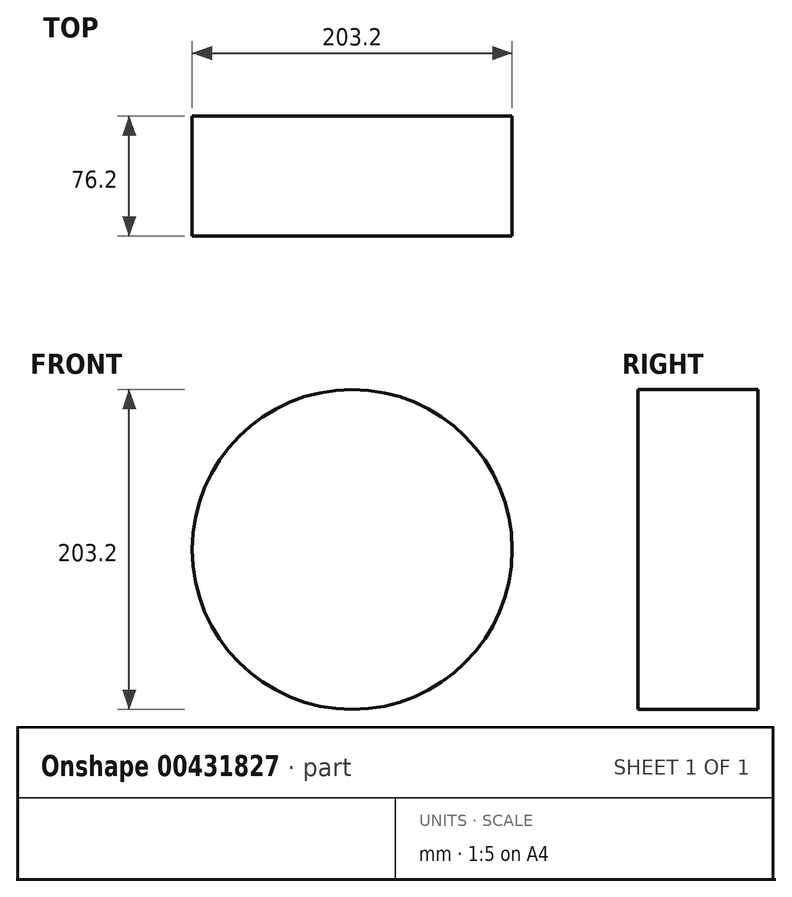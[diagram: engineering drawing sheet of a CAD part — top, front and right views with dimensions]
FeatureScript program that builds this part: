
annotation { "Feature Type Name" : "Feature", "Feature Type Description" : "" }
export const myFeature = defineFeature(function(context is Context, id is Id, definition is map)
    precondition{}
    {
        {
            var Q0;
            Q0=qCreatedBy(makeId("Front.planeOp"),FACE);
            var sketch = newSketch(context, id + "F0", { "sketchPlane" : qUnion([Q0])});
            skCircle(sketch, "E0", {"center": v(0, 0) * mm, "radius": 101.6 * mm});
            skSolve(sketch);
        }
        {
            var Q0;
            Q0=sQuery(id+"F0.wireOp",EDGE,"E0");
            extrude(context, id + "F1", {"bodyType" : ToolBodyType.SURFACE, "surfaceEntities" : qUnion([Q0]), "depth" : 76.2 * mm});
        }
    });
